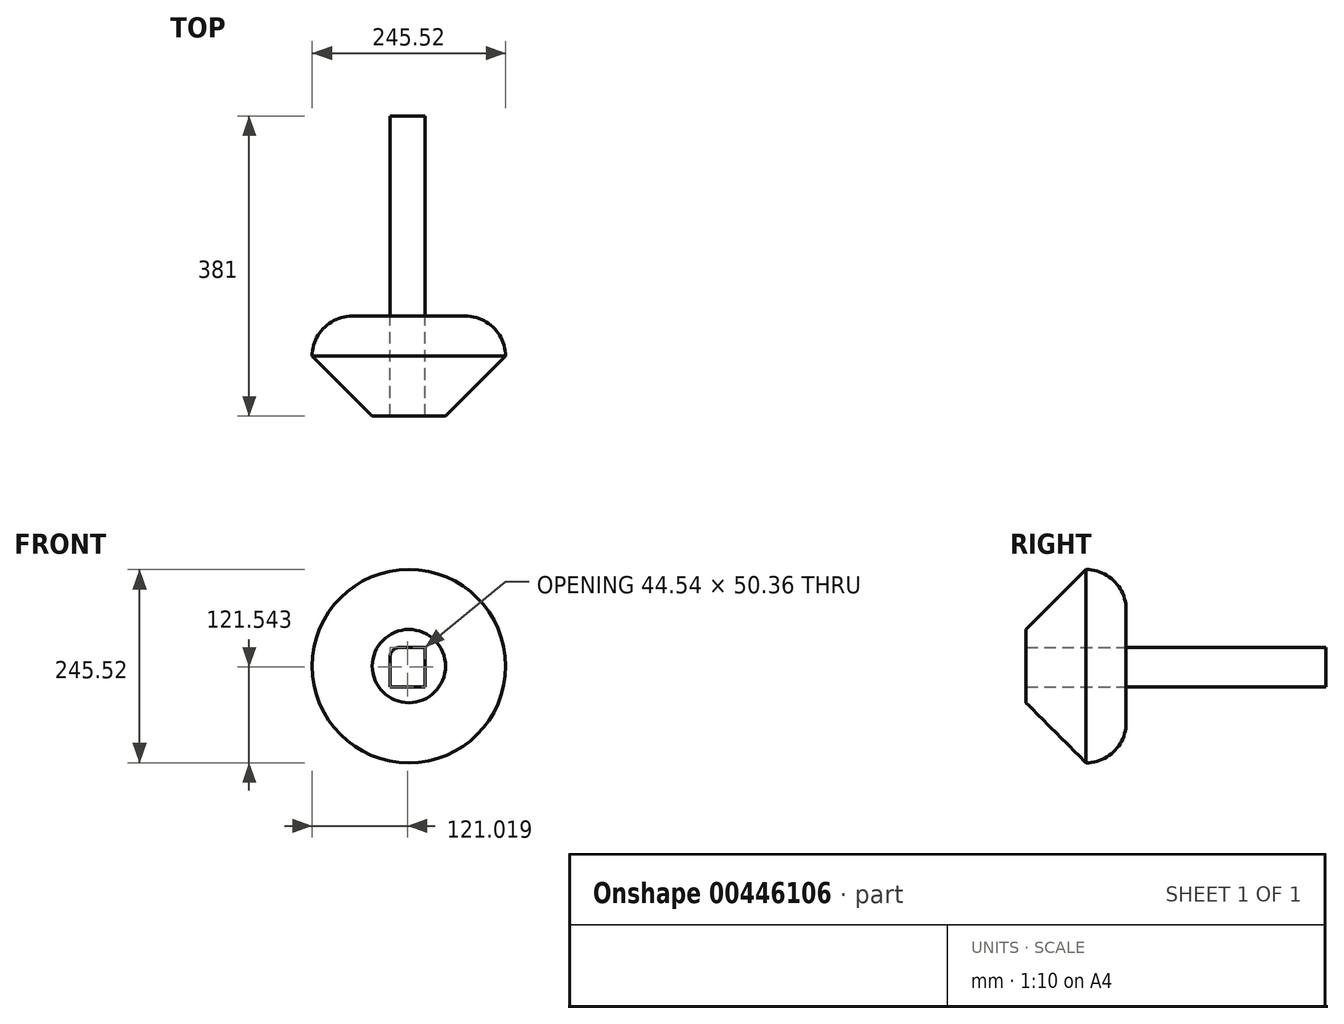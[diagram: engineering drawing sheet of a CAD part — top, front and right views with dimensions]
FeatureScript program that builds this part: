
annotation { "Feature Type Name" : "Feature", "Feature Type Description" : "" }
export const myFeature = defineFeature(function(context is Context, id is Id, definition is map)
    precondition{}
    {
        {
            var Q0;
            Q0=qCreatedBy(makeId("Front.planeOp"),FACE);
            var sketch = newSketch(context, id + "F0", { "sketchPlane" : qUnion([Q0])});
            skCircle(sketch, "E0", {"center": v(0, 0) * mm, "radius": 122.76 * mm});
            skLineSegment(sketch, "E1.bottom", {"start": v(-24.01, 23.96) * mm, "end": v(20.53, 23.96) * mm});
            skLineSegment(sketch, "E1.top", {"start": v(-24.01, -26.4) * mm, "end": v(20.53, -26.4) * mm});
            skLineSegment(sketch, "E1.left", {"start": v(-24.01, 23.96) * mm, "end": v(-24.01, -26.4) * mm});
            skLineSegment(sketch, "E1.right", {"start": v(20.53, 23.96) * mm, "end": v(20.53, -26.4) * mm});
            skSolve(sketch);
        }
        {
            var Q0;
            Q0=makeQuery(id+"F0.imprint","IMPRINT",FACE,{"disambiguationData":[TD([[makeQuery(id+"F0.imprint","IMPRINT",EDGE,{"derivedFrom":sQuery(id+"F0.wireOp",EDGE,"E0")}),1.0]])]});
            extrude(context, id + "F1", {"entities" : qUnion([Q0]), "depth" : 127 * mm});
        }
        {
            var Q0;
            Q0=makeQuery(id+"F1.opExtrude","CAP_EDGE",EDGE,{"disambiguationData":[OSD([sQuery(id+"F0.wireOp",EDGE,"E0")])],"isStart":true});
            fillet(context, id + "F2", {"entities" : qUnion([Q0]), "radius" : 50.8 * mm, "tangentPropagation" : true, "allowEdgeOverflow" : false});
        }
        {
            var Q0;
            Q0=makeQuery(id+"F1.opExtrude","CAP_EDGE",EDGE,{"disambiguationData":[OSD([sQuery(id+"F0.wireOp",EDGE,"E0")])],"isStart":false});
            chamfer(context, id + "F3", {"entities" : qUnion([Q0]), "width" : 76.2 * mm, "tangentPropagation" : true});
        }
        {
            var Q0;
            Q0=makeQuery(id+"F1.opExtrude","SWEPT_EDGE",EDGE,{"disambiguationData":[OSD([sQuery(id+"F0.wireOp",EDGE,"E1.bottom"),sQuery(id+"F0.wireOp",EDGE,"E1.left")])]});
            fillet(context, id + "F4", {"entities" : qUnion([Q0]), "radius" : 12.7 * mm, "tangentPropagation" : true, "allowEdgeOverflow" : false});
        }
        {
            var Q0;
            Q0=makeQuery(id+"F1.opExtrude","CAP_FACE",FACE,{"disambiguationData":[OSD([sQuery(id+"F0.wireOp",EDGE,"E0"),sQuery(id+"F0.wireOp",EDGE,"E1.bottom"),sQuery(id+"F0.wireOp",EDGE,"E1.top"),sQuery(id+"F0.wireOp",EDGE,"E1.left"),sQuery(id+"F0.wireOp",EDGE,"E1.right")])],"isStart":true});
            var sketch = newSketch(context, id + "F5", { "sketchPlane" : qUnion([Q0])});
            skCircle(sketch, "E2", {"center": v(0, 0) * mm, "radius": 97.22 * mm});
            skSolve(sketch);
        }
        {
            var Q0;
            {var subQ3=sQuery(id+"F0.wireOp",EDGE,"E1.top");Q0=makeQuery(id+"F5.imprint","IMPRINT",FACE,{"disambiguationData":[TD([[makeQuery(id+"F5.imprint","IMPRINT",EDGE,{"derivedFrom":makeQuery(id+"F1.opExtrude","CAP_EDGE",EDGE,{"disambiguationData":[OSD([subQ3])],"isStart":true})}),-1.0]])]});}
            extrude(context, id + "F6", {"entities" : qUnion([Q0]), "depth" : 254 * mm});
        }
    });
